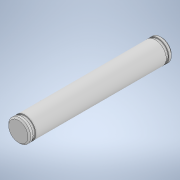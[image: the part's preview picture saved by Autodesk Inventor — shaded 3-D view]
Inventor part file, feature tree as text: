
AUTODESK INVENTOR PART (.ipt)
format: ipt  version: 2022 (Build 260153000, 153)  size: 124,416 bytes
history: native  units: mm
features: revolve x1, chamfer x1, sketch x1
ambient origin geometry x8: Origin, YZ Plane, XZ Plane, XY Plane, X Axis, Y Axis, Z Axis, Center Point
bodies: Solid1 (feature_tree)
feature tree (3):
  revolve  "Revolution1"  [1 undecoded]
  chamfer  "Chamfer1"  Distance=1.5mm
  sketch  "Sketch1"  dims[d0=6.0mm d3=71.0mm d4=1.5mm d5=0.5mm d6=1.5mm d7=2.0mm d8=2.0mm d9=90.0deg d10=0.75mm d11=2.0mm d12=45.0deg]
note: 1 required parameter value undecoded (feature->parameter linkage not recoverable at this tier; creation-order binding heuristic only, values carry confidence <= 0.55)
